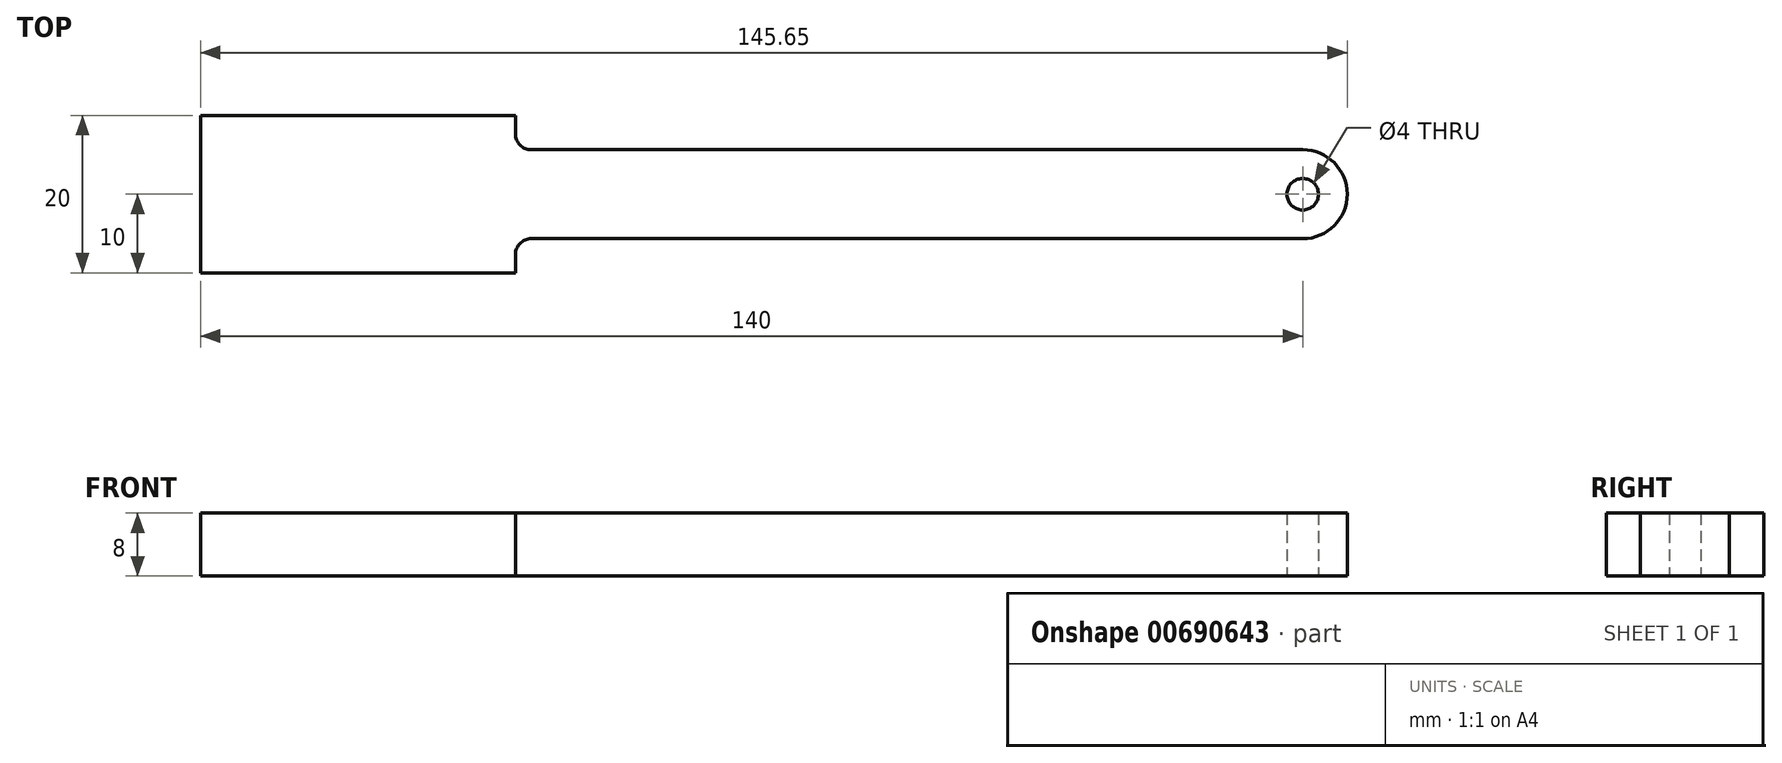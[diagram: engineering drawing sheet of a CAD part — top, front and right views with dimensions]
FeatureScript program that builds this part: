
annotation { "Feature Type Name" : "Feature", "Feature Type Description" : "" }
export const myFeature = defineFeature(function(context is Context, id is Id, definition is map)
    precondition{}
    {
        {
            var Q0;
            Q0=qCreatedBy(makeId("Top.planeOp"),FACE);
            var sketch = newSketch(context, id + "F0", { "sketchPlane" : qUnion([Q0])});
            skLineSegment(sketch, "E0.bottom", {"start": v(20, -10) * mm, "end": v(-20, -10) * mm});
            skLineSegment(sketch, "E0.top", {"start": v(20, 10) * mm, "end": v(-20, 10) * mm});
            skLineSegment(sketch, "E0.left", {"start": v(20, 7.65) * mm, "end": v(20, 10) * mm});
            skLineSegment(sketch, "E0.right", {"start": v(-20, -10) * mm, "end": v(-20, 10) * mm});
            skPoint(sketch, "E0.middle", {"position": v(0, 0) * mm});
            skLineSegment(sketch, "E1.bottom", {"start": v(22, -5.65) * mm, "end": v(120, -5.65) * mm});
            skLineSegment(sketch, "E1.top", {"start": v(22, 5.65) * mm, "end": v(120, 5.65) * mm});
            skCircle(sketch, "E2", {"center": v(120, 0) * mm, "radius": 5.65 * mm});
            skCircle(sketch, "E3", {"center": v(120, 0) * mm, "radius": 2 * mm});
            skArc(sketch, "E4.filletArc", {"start": v(20, 7.65) * mm, "mid": v(20.59, 6.24) * mm, "end": v(22, 5.65) * mm});
            skLineSegment(sketch, "E5", {"start": v(20, -7.65) * mm, "end": v(20, -10) * mm});
            skPoint(sketch, "E6.visualSharp", {"position": v(20, -5.65) * mm});
            skArc(sketch, "E6.filletArc", {"start": v(22, -5.65) * mm, "mid": v(20.59, -6.24) * mm, "end": v(20, -7.65) * mm});
            skSolve(sketch);
        }
        {
            var Q0;
            Q0 = qSketchRegion(id + "F0", true);
            extrude(context, id + "F1", {"entities" : qUnion([Q0]), "depth" : 8 * mm, "offsetDistance" : 25 * mm});
        }
    });
